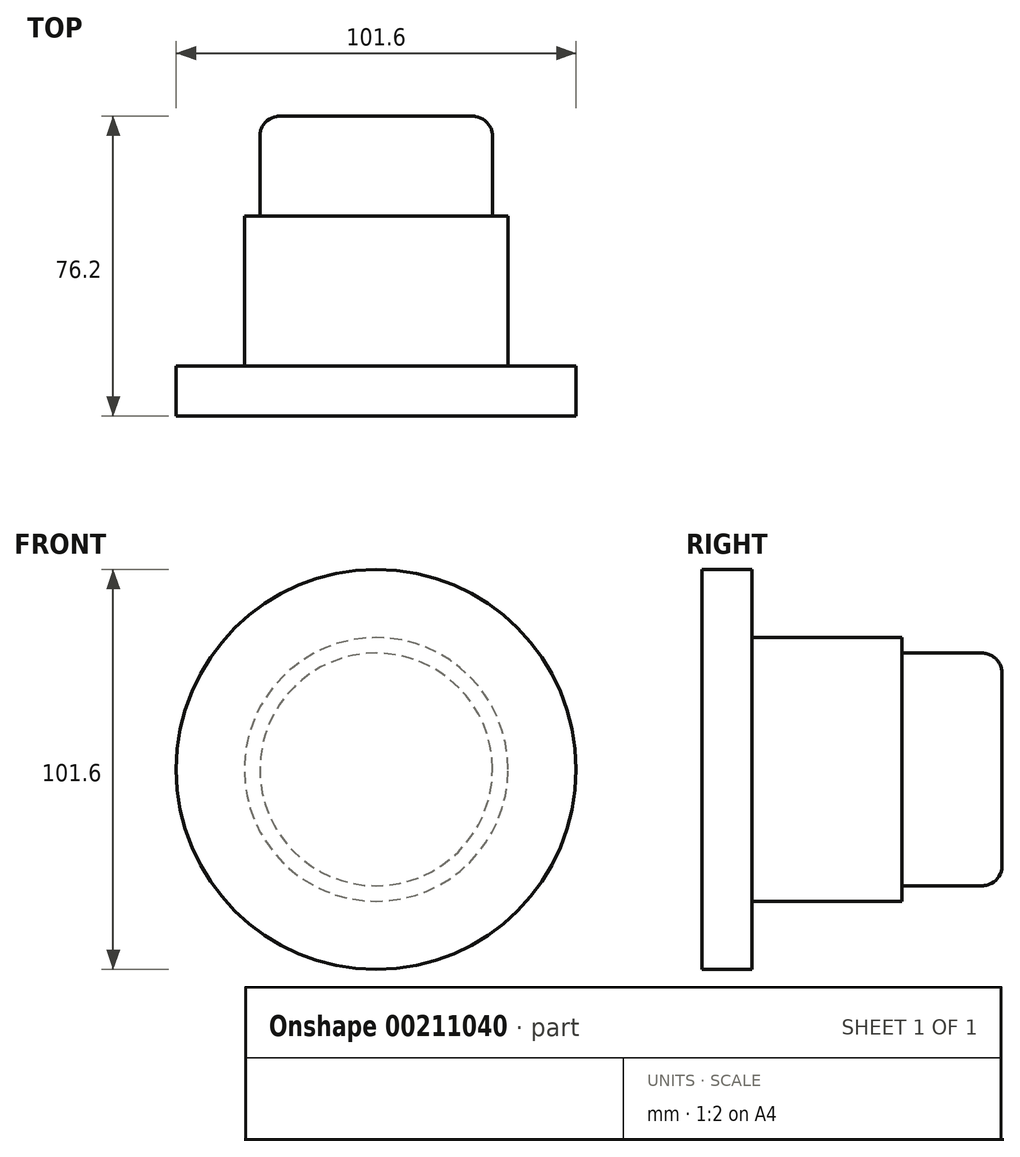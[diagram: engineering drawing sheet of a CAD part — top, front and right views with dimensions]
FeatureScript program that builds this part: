
annotation { "Feature Type Name" : "Feature", "Feature Type Description" : "" }
export const myFeature = defineFeature(function(context is Context, id is Id, definition is map)
    precondition{}
    {
        {
            var Q0;
            Q0=qCreatedBy(makeId("Front.planeOp"),FACE);
            var sketch = newSketch(context, id + "F0", { "sketchPlane" : qUnion([Q0])});
            skCircle(sketch, "E0", {"center": v(0, 0) * mm, "radius": 50.8 * mm});
            skSolve(sketch);
        }
        {
            var Q0;
            Q0 = qSketchRegion(id + "F0", true);
            extrude(context, id + "F1", {"entities" : qUnion([Q0]), "depth" : 12.7 * mm});
        }
        {
            var Q0;
            Q0=qCreatedBy(makeId("Front.planeOp"),FACE);
            var sketch = newSketch(context, id + "F2", { "sketchPlane" : qUnion([Q0])});
            skCircle(sketch, "E1", {"center": v(0, 0) * mm, "radius": 33.5 * mm});
            skSolve(sketch);
        }
        {
            var Q0;
            Q0 = qSketchRegion(id + "F2", true);
            extrude(context, id + "F3", {"entities" : qUnion([Q0]), "operationType" : NewBodyOperationType.ADD, "oppositeDirection" : true, "depth" : 38.1 * mm});
        }
        {
            var Q0;
            Q0=makeQuery(id+"F3.opExtrude","CAP_FACE",FACE,{"disambiguationData":[OSD([sQuery(id+"F2.wireOp",EDGE,"E1")])],"isStart":false});
            var sketch = newSketch(context, id + "F4", { "sketchPlane" : qUnion([Q0])});
            skCircle(sketch, "E2", {"center": v(0, 0) * mm, "radius": 29.55 * mm});
            skSolve(sketch);
        }
        {
            var Q0;
            Q0 = qSketchRegion(id + "F4", true);
            extrude(context, id + "F5", {"entities" : qUnion([Q0]), "operationType" : NewBodyOperationType.ADD, "depth" : 25.4 * mm});
        }
        {
            var Q0;
            Q0=makeQuery(id+"F5.opExtrude","CAP_EDGE",EDGE,{"disambiguationData":[OSD([sQuery(id+"F4.wireOp",EDGE,"E2")])],"isStart":false});
            fillet(context, id + "F6", {"entities" : qUnion([Q0]), "radius" : 5.08 * mm, "tangentPropagation" : true, "allowEdgeOverflow" : false});
        }
    });
